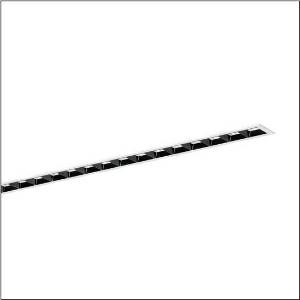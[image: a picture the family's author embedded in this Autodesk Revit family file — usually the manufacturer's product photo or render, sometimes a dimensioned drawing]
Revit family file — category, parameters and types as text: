
# Revit family: silica_r__21_51mx14dc4awb_d642
name_source: partatom
category: Lighting Fixtures
units: mm (PartAtom-declared; Revit-internal decimal feet)

## family parameters
Cut with Voids When Loaded = No
Host = Face
Light Source = No
Part Type = Normal
Room Calculation Point = No
Round Connector Dimension = Use Diameter
Shared = No

## types (1)
- --- (1 x LED, 10800 lm, 73.7 W, 4000K)
    Apparent Load = 74 VA
    CIE Flux Codes = 74 94 99 100 100
    Color Rendering = 80
    Color Temperature = 4000K
    Default Elevation = 1800 mm
    Description = Silica® 21, office luminaire, primary light control with darklight reflector, of PMMA, black, light emission: direct distribution, primary light characteristic: asymmetric, installation type: recessed, LED, rated luminous flux: 10.800lm, luminous efficacy: 147lm/W, light colour: 840, colour temperature: 4000K, with terminal, 3+2-pole, max. 2.5mm², mains connection: 220..240V, AC, 50/60Hz, rated input power: 73.7W, luminaire housing, of aluminium, traffic white (RAL 9016), length: 3.028mm, width: 79mm, height: 53mm, protection rating (complete): IP20, insulation class (complete): insulation class I (protective earthing), certification: CE, permissible operating ambient temperature: 0..+35°C, standard: EN 50419, packaging unit: 1 piece
    Height = 0 mm  [stored 0 ft]
    Lamp = 1 x LED
    Lamp Light Flux = 10800 lm
    Lamp Power = 73.7 W
    Lamp count = 1
    Length = 3027 mm
    Luminous efficacy = 147 lm/W
    Manufacturer = Siteco
    ModVariant = No
    Model = 51MX14DC4AWB
    Mounting Place = Ceiling
    Mounting Type = Recessed
    Number of Poles = 1
    OnlyDefault = Yes
    Power Factor = 1
    Product Name = Silica® 21
    Product group = office luminaire | ceiling recessed
    ProductGroupID = 400
    Protection Class = Protection class I
    Protection Degree = IP 20
    RLX_Detail_Level = 1
    RlxData = <blob elided: 62805 chars, md5=183664ac>
    Socket = socket
    Standby Power = 0 W
    System Light Flux = 10800 lm
    System Power = 74 W
    Type Comments = factory setting: luminous flux: 100 % | dim-lin: 254 | 418 mA
    Type Image = l_1251632.jpg
    URL = http://relux.com
    VarID = @adj_031547
    Voltage = 0 V
    Weight = 0.00 kg
    Width = 79 mm

note: [stored X ft] marks values corroborated as IEEE doubles in the binary element streams (Revit-internal decimal feet)

## geometry (parser evidence)
native form markers: Blend x4, Sweep x11
no freeform markers — native parametric forms only
